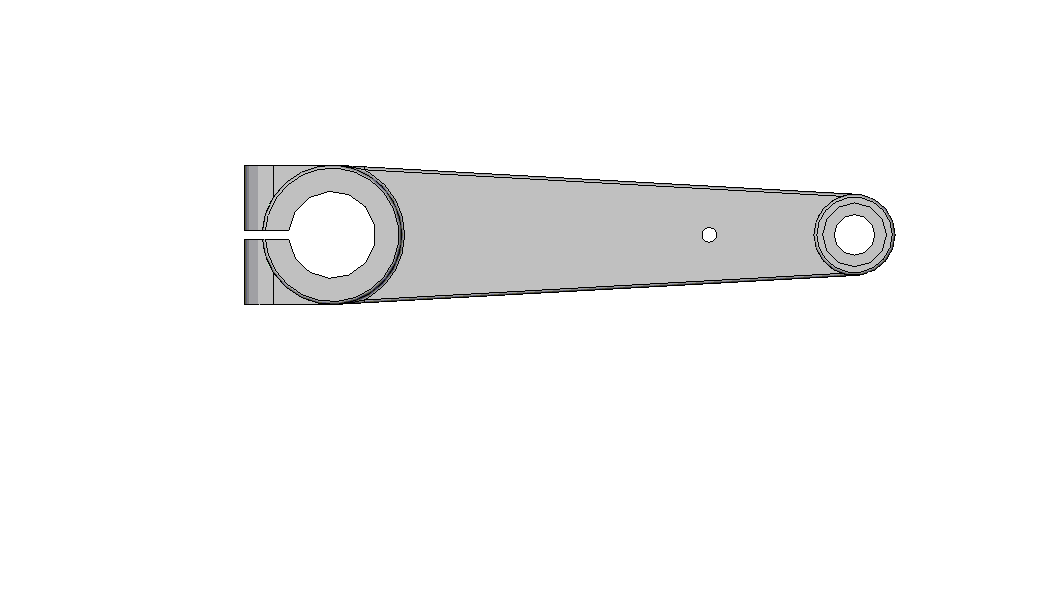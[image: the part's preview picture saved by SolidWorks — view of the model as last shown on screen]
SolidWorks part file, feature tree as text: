
SOLIDWORKS PART (.sldprt)
format: sldprt  version: not decoded by parser v0  size: 376,832 bytes
history: native  units: mm
features: sketch x10, extrude x6, fillet x5, cut_extrude x5, plane x4, mirror x2, material x1 (+8 scaffold rows collapsed)
feature tree (41):
  scaffold x8  (default folders/planes/origin — collapsed)
  material  "Matériau <non spécifié>"
  plane  "Face"
  plane  "Dessus"
  plane  "Droite"
  sketch  "Esquisse1"  dims[D1=30.0mm D2=48.0mm]
  extrude  "Extrusion1"  Depth=2mm
  sketch  "Esquisse2"  dims[D1=14.0mm D2=28.0mm D3=180.0mm]
  extrude  "Extrusion2"  Depth=2mm
  sketch  "Esquisse3"
  extrude  "Extrusion3"  Depth=7.5mm
  sketch  "Esquisse4"  dims[D1=36.0mm D2=14.0mm]
  extrude  "Extrusion4"  Depth=8mm
  mirror  "Symétrie1"
  mirror  "Dépouille3"
  fillet  "Congé11"  Radius=1mm
  sketch  "Esquisse5"  dims[D7=20.0mm D8=20.0mm D1=20.0mm D2=20.0mm D3=2.0mm D4=20.0mm D5=10.0mm D6=10.0mm]
  extrude  "Extrusion5"  Depth=24mm
  sketch  "Esquisse6"  dims[D1=30.0mm D3=14.0mm D4=10.0mm D2=3.0mm]
  cut_extrude  "Enlèv. mat.-Extru.1"  [1 undecoded]
  sketch  "Esquisse7"  dims[D1=10.5mm D2=10.5mm]
  cut_extrude  "Enlèv. mat.-Extru.2"  [1 undecoded]
  sketch  "Esquisse10"  dims[D1=22.0mm]
  cut_extrude  "Enlèv. mat.-Extru.4"  Depth=5mm
  fillet  "Congé16"  Radius=2mm
  fillet  "Congé17"  Radius=2mm
  fillet  "Congé25"  Radius=1mm
  fillet  "Congé30"  Radius=1mm
  plane  "Plan2"
  sketch  "Esquisse13"  dims[D2=10.0mm D1=25.75mm]
  cut_extrude  "Enlèv. mat.-Extru.6"  [1 undecoded]
  extrude  "Symétrie2"  [1 undecoded]
  sketch  "Esquisse14"  dims[D1=5.1mm D2=130.0mm]
  cut_extrude  "Enlèv. mat.-Extru.7"  [1 undecoded]
decode coverage: 20 of 28 modeling features carry decoded parameters
note: 5 parameter values undecoded
summary: no parameter record found for 5 features
note: suppression state not decoded; provenance and decode notes live in map.json
